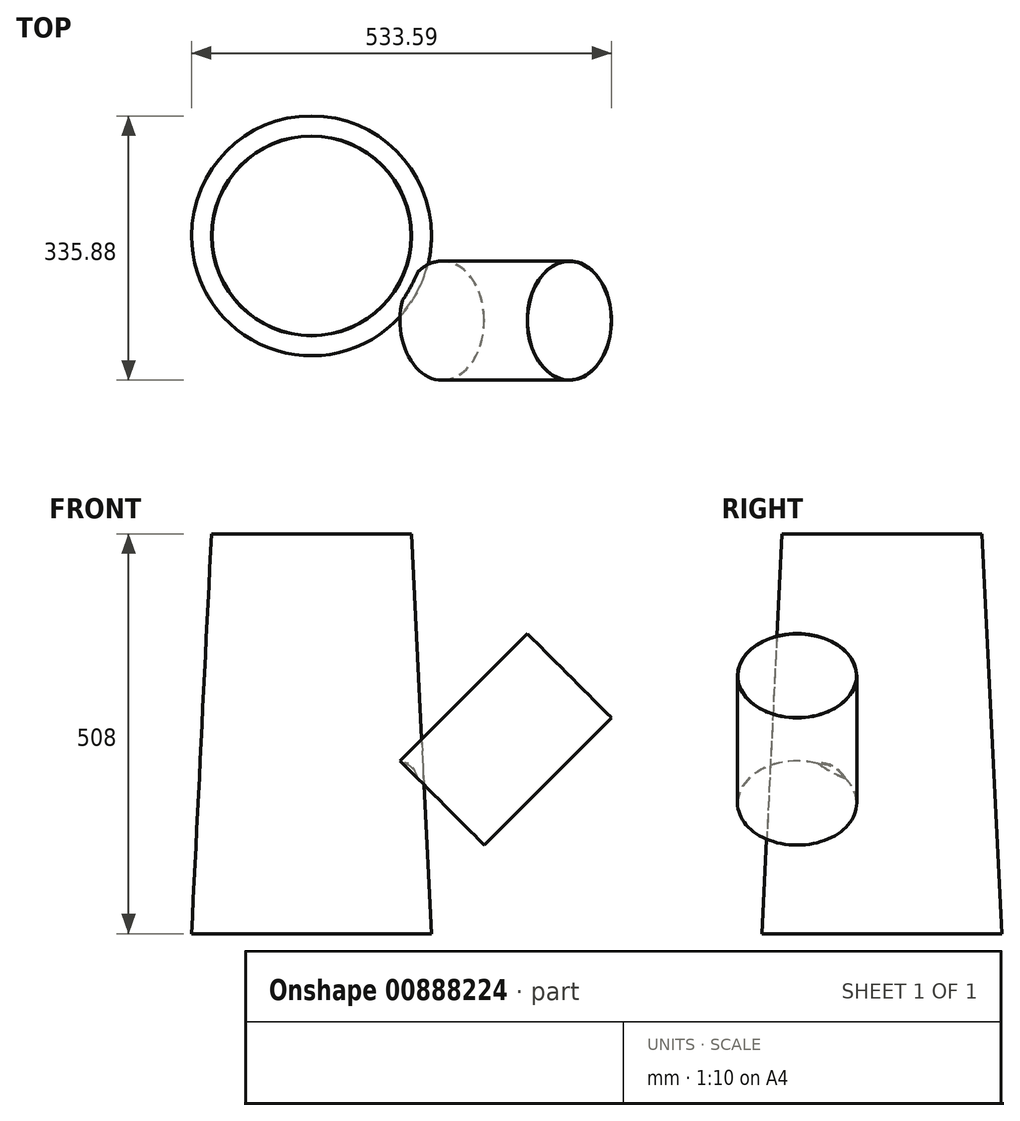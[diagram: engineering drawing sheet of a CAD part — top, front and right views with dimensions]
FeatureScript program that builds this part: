
annotation { "Feature Type Name" : "Feature", "Feature Type Description" : "" }
export const myFeature = defineFeature(function(context is Context, id is Id, definition is map)
    precondition{}
    {
        {
            var Q0;
            Q0=qCreatedBy(makeId("Front.planeOp"),FACE);
            var sketch = newSketch(context, id + "F0", { "sketchPlane" : qUnion([Q0])});
            skLineSegment(sketch, "E0", {"start": v(0, 0) * mm, "end": v(0, 508) * mm});
            skLineSegment(sketch, "E1", {"start": v(0, 508) * mm, "end": v(0, 254) * mm});
            skPoint(sketch, "E2", {"position": v(251.45, 403.85) * mm});
            skPoint(sketch, "E3", {"position": v(125.72, 278.12) * mm});
            skLineSegment(sketch, "E4", {"start": v(125.72, 278.12) * mm, "end": v(251.45, 403.85) * mm});
            skPoint(sketch, "E5.start.orphan", {"position": v(0, 152.4) * mm});
            skLineSegment(sketch, "E6", {"start": v(125.72, 278.12) * mm, "end": v(0, 152.4) * mm});
            skSolve(sketch);
        }
        {
            var Q0;
            Q0=sQuery(id+"F0.wireOp",VERTEX,"E0.start");
            var Q1;
            Q1=sQuery(id+"F0.wireOp",EDGE,"E0");
            cPlane(context, id + "F1", {"entities" : qUnion([Q0, Q1]), "cplaneType" : CPlaneType.LINE_POINT, "offset" : 25.4 * mm, "width" : 152.4 * mm, "height" : 152.4 * mm});
        }
        {
            var Q0;
            Q0=sQuery(id+"F0.wireOp",VERTEX,"E0.end");
            var Q1;
            Q1=sQuery(id+"F0.wireOp",EDGE,"E1");
            cPlane(context, id + "F2", {"entities" : qUnion([Q0, Q1]), "cplaneType" : CPlaneType.LINE_POINT, "offset" : 25.4 * mm, "width" : 152.4 * mm, "height" : 152.4 * mm});
        }
        {
            var Q0;
            Q0=sQuery(id+"F0.wireOp",VERTEX,"E2");
            var Q1;
            Q1=sQuery(id+"F0.wireOp",EDGE,"E4");
            cPlane(context, id + "F3", {"entities" : qUnion([Q0, Q1]), "cplaneType" : CPlaneType.LINE_POINT, "offset" : 25.4 * mm, "width" : 152.4 * mm, "height" : 152.4 * mm});
        }
        {
            var Q0;
            Q0=qCreatedBy(id+"F1.planeOp",FACE);
            var sketch = newSketch(context, id + "F4", { "sketchPlane" : qUnion([Q0])});
            skCircle(sketch, "E7", {"center": v(0, 0) * mm, "radius": 152.4 * mm});
            skSolve(sketch);
        }
        {
            var Q0;
            Q0=qCreatedBy(id+"F2.planeOp",FACE);
            var sketch = newSketch(context, id + "F5", { "sketchPlane" : qUnion([Q0])});
            skCircle(sketch, "E8", {"center": v(0, 0) * mm, "radius": 127 * mm});
            skSolve(sketch);
        }
        {
            var Q0;
            Q0=makeQuery(id+"F4.imprint","IMPRINT",FACE,{"disambiguationData":[TD([[makeQuery(id+"F4.imprint","IMPRINT",EDGE,{"derivedFrom":sQuery(id+"F4.wireOp",EDGE,"E7")}),1.0]])]});
            var Q1;
            Q1=makeQuery(id+"F5.imprint","IMPRINT",FACE,{"disambiguationData":[TD([[makeQuery(id+"F5.imprint","IMPRINT",EDGE,{"derivedFrom":sQuery(id+"F5.wireOp",EDGE,"E8")}),1.0]])]});
            var Q2;
            Q2=sQuery(id+"F4.wireOp",EDGE,"E7");
            var Q3;
            Q3=sQuery(id+"F5.wireOp",EDGE,"E8");
            loft(context, id + "F6", {"sheetProfilesArray" : [{ "sheetProfileEntities" : qUnion([Q0]) }, { "sheetProfileEntities" : qUnion([Q1]) }], "wireProfilesArray" : [{ "wireProfileEntities" : qUnion([Q2]) }, { "wireProfileEntities" : qUnion([Q3]) }]});
        }
        {
            var Q0;
            Q0=qCreatedBy(id+"F3.planeOp",FACE);
            var sketch = newSketch(context, id + "F7", { "sketchPlane" : qUnion([Q0])});
            skPoint(sketch, "E9", {"position": v(-107.76, 0) * mm});
            skCircle(sketch, "E10", {"center": v(-107.76, 0) * mm, "radius": 76.2 * mm});
            skCircle(sketch, "E11", {"center": v(-107.76, 0) * mm, "radius": 75.72 * mm});
            skSolve(sketch);
        }
        {
            var Q0;
            Q0=makeQuery(id+"F6.opLoft","CAP_FACE",FACE,{"disambiguationData":[OSD([makeQuery(id+"F5.imprint","IMPRINT",FACE,{"disambiguationData":[TD([[makeQuery(id+"F5.imprint","IMPRINT",EDGE,{"derivedFrom":sQuery(id+"F5.wireOp",EDGE,"E8")}),1.0]])]})])],"isStart":true});
            var sketch = newSketch(context, id + "F8", { "sketchPlane" : qUnion([Q0])});
            skCircle(sketch, "E12", {"center": v(0, 0) * mm, "radius": 126.52 * mm});
            skSolve(sketch);
        }
        {
            var Q0;
            Q0=makeQuery(id+"F6.opLoft","CAP_FACE",FACE,{"disambiguationData":[OSD([makeQuery(id+"F4.imprint","IMPRINT",FACE,{"disambiguationData":[TD([[makeQuery(id+"F4.imprint","IMPRINT",EDGE,{"derivedFrom":sQuery(id+"F4.wireOp",EDGE,"E7")}),1.0]])]})])],"isStart":true});
            var sketch = newSketch(context, id + "F9", { "sketchPlane" : qUnion([Q0])});
            skCircle(sketch, "E13", {"center": v(0.1, 0) * mm, "radius": 151.82 * mm});
            skSolve(sketch);
        }
        {
            var Q0;
            Q0=makeQuery(id+"F7.imprint","IMPRINT",FACE,{"disambiguationData":[TD([[makeQuery(id+"F7.imprint","IMPRINT",EDGE,{"derivedFrom":sQuery(id+"F7.wireOp",EDGE,"E11")}),1.0]])]});
            extrude(context, id + "F10", {"entities" : qUnion([Q0]), "operationType" : NewBodyOperationType.ADD, "oppositeDirection" : true, "depth" : 228.6 * mm, "offsetDistance" : 25.4 * mm});
        }
        {
            var Q0;
            Q0=makeQuery(id+"F10.opExtrude","CAP_FACE",FACE,{"disambiguationData":[OSD([sQuery(id+"F7.wireOp",EDGE,"E11")])],"isStart":true});
            var sketch = newSketch(context, id + "F11", { "sketchPlane" : qUnion([Q0])});
            skCircle(sketch, "E14", {"center": v(-107.76, 0) * mm, "radius": 75.23 * mm});
            skSolve(sketch);
        }
        {
            var Q0;
            Q0=makeQuery(id+"F11.imprint","IMPRINT",FACE,{"disambiguationData":[TD([[makeQuery(id+"F11.imprint","IMPRINT",EDGE,{"derivedFrom":sQuery(id+"F11.wireOp",EDGE,"E14")}),1.0]])]});
            extrude(context, id + "F12", {"entities" : qUnion([Q0]), "operationType" : NewBodyOperationType.REMOVE, "oppositeDirection" : true, "depth" : 228.6 * mm, "offsetDistance" : 25.4 * mm});
        }
        {
            var Q1;
            Q1 = qSketchRegion(id + "F8", true);
            var Q2;
            Q2 = qSketchRegion(id + "F9", true);
            loft(context, id + "F13", {"operationType" : NewBodyOperationType.REMOVE, "sheetProfilesArray" : [{ "sheetProfileEntities" : qUnion([Q1]) }, { "sheetProfileEntities" : qUnion([Q2]) }]});
        }
    });
